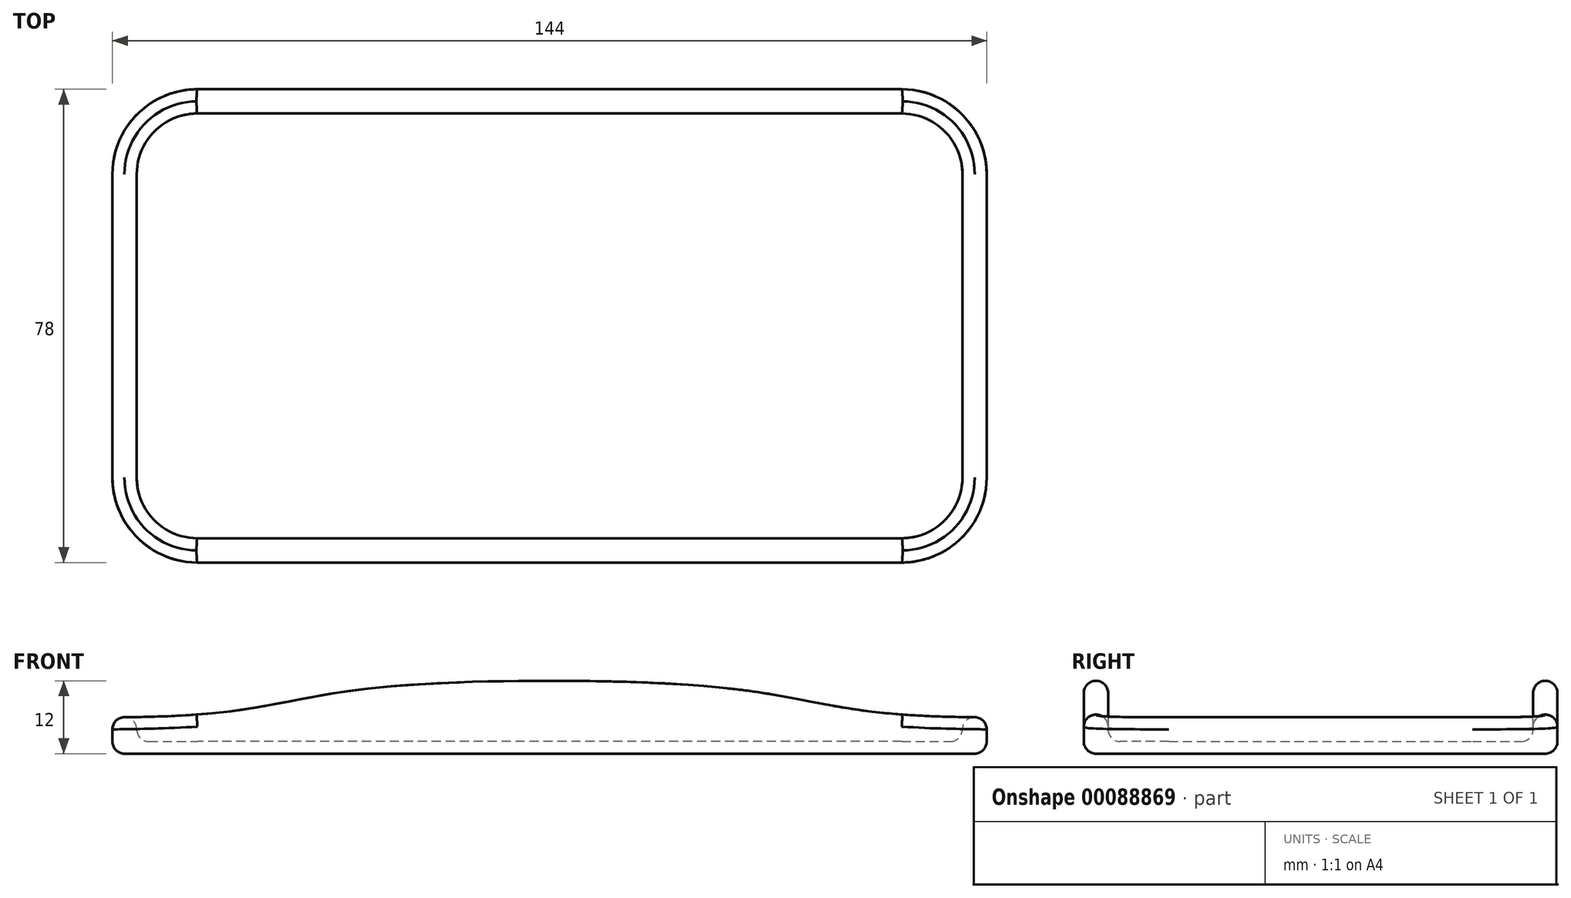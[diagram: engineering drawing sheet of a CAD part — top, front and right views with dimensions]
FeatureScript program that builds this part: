
annotation { "Feature Type Name" : "Feature", "Feature Type Description" : "" }
export const myFeature = defineFeature(function(context is Context, id is Id, definition is map)
    precondition{}
    {
        {
            var Q0;
            Q0=qCreatedBy(makeId("Top.planeOp"),FACE);
            var sketch = newSketch(context, id + "F0", { "sketchPlane" : qUnion([Q0])});
            skLineSegment(sketch, "E0.bottom", {"start": v(58, -35) * mm, "end": v(-58, -35) * mm});
            skLineSegment(sketch, "E0.top", {"start": v(58, 35) * mm, "end": v(-58, 35) * mm});
            skLineSegment(sketch, "E0.left", {"start": v(68, -25) * mm, "end": v(68, 25) * mm});
            skLineSegment(sketch, "E0.right", {"start": v(-68, -25) * mm, "end": v(-68, 25) * mm});
            skPoint(sketch, "E0.middle", {"position": v(0, 0) * mm});
            skPoint(sketch, "E1.visualSharp", {"position": v(-68, 35) * mm});
            skArc(sketch, "E1.filletArc", {"start": v(-58, 35) * mm, "mid": v(-65.07, 32.07) * mm, "end": v(-68, 25) * mm});
            skPoint(sketch, "E2.visualSharp", {"position": v(68, 35) * mm});
            skArc(sketch, "E2.filletArc", {"start": v(68, 25) * mm, "mid": v(65.07, 32.07) * mm, "end": v(58, 35) * mm});
            skPoint(sketch, "E3.visualSharp", {"position": v(68, -35) * mm});
            skArc(sketch, "E3.filletArc", {"start": v(58, -35) * mm, "mid": v(65.07, -32.07) * mm, "end": v(68, -25) * mm});
            skPoint(sketch, "E4.visualSharp", {"position": v(-68, -35) * mm});
            skArc(sketch, "E4.filletArc", {"start": v(-68, -25) * mm, "mid": v(-65.07, -32.07) * mm, "end": v(-58, -35) * mm});
            skArc(sketch, "E5.0", {"start": v(72, 25) * mm, "mid": v(67.9, 34.9) * mm, "end": v(58, 39) * mm});
            skLineSegment(sketch, "E5.1", {"start": v(72, -25) * mm, "end": v(72, 25) * mm});
            skLineSegment(sketch, "E5.2", {"start": v(58, 39) * mm, "end": v(-58, 39) * mm});
            skArc(sketch, "E5.3", {"start": v(58, -39) * mm, "mid": v(67.9, -34.9) * mm, "end": v(72, -25) * mm});
            skArc(sketch, "E5.4", {"start": v(-58, 39) * mm, "mid": v(-67.9, 34.9) * mm, "end": v(-72, 25) * mm});
            skLineSegment(sketch, "E5.5", {"start": v(-72, -25) * mm, "end": v(-72, 25) * mm});
            skArc(sketch, "E5.6", {"start": v(-72, -25) * mm, "mid": v(-67.9, -34.9) * mm, "end": v(-58, -39) * mm});
            skLineSegment(sketch, "E5.7", {"start": v(58, -39) * mm, "end": v(-58, -39) * mm});
            skSolve(sketch);
        }
        {
            var Q0;
            Q0=makeQuery(id+"F0.imprint","IMPRINT",FACE,{"disambiguationData":[TD([[makeQuery(id+"F0.imprint","IMPRINT",EDGE,{"derivedFrom":sQuery(id+"F0.wireOp",EDGE,"E0.bottom")}),-1.0]])]});
            extrude(context, id + "F1", {"entities" : qUnion([Q0]), "depth" : 2 * mm});
        }
        {
            var Q0;
            Q0=makeQuery(id+"F0.imprint","IMPRINT",FACE,{"disambiguationData":[TD([[makeQuery(id+"F0.imprint","IMPRINT",EDGE,{"derivedFrom":sQuery(id+"F0.wireOp",EDGE,"E0.bottom")}),1.0]])]});
            extrude(context, id + "F2", {"entities" : qUnion([Q0]), "operationType" : NewBodyOperationType.ADD, "depth" : 12 * mm});
        }
        {
            var Q0;
            Q0=qCreatedBy(makeId("Front.planeOp"),FACE);
            var sketch = newSketch(context, id + "F3", { "sketchPlane" : qUnion([Q0])});
            skLineSegment(sketch, "E6.0", {"start": v(58, 12) * mm, "end": v(-58, 12) * mm});
            skLineSegment(sketch, "E7.0", {"start": v(72, 0) * mm, "end": v(-72, 0) * mm});
            skLineSegment(sketch, "E8.0", {"start": v(72, 12) * mm, "end": v(72, 0) * mm});
            skLineSegment(sketch, "E9.0", {"start": v(-72, 12) * mm, "end": v(-72, 0) * mm});
            skFitSpline(sketch, "E10", {"points": [v(-72, 6) * mm, v(0, 12) * mm], "startDerivative": vector(102.55, 0) * mm, "endDerivative": vector(141.46, 0) * mm});
            skLineSegment(sketch, "E11", {"start": v(0, 12) * mm, "end": v(0, 0) * mm, "construction": true});
            skFitSpline(sketch, "E12.MirrorCS", {"points": [v(72, 6) * mm, v(0, 12) * mm], "startDerivative": vector(-102.55, 0) * mm, "endDerivative": vector(-141.46, 0) * mm});
            skPoint(sketch, "E13.orphan", {"position": v(-58, 0) * mm});
            skPoint(sketch, "E14.orphan", {"position": v(58, 0) * mm});
            skSolve(sketch);
        }
        {
            var Q0;
            {var subQ2=sQuery(id+"F3.wireOp",EDGE,"E7.0");Q0=makeQuery(id+"F3.imprint","IMPRINT",FACE,{"disambiguationData":[TD([[makeQuery(id+"F3.imprint","IMPRINT",EDGE,{"derivedFrom":subQ2}),-1.0]])]});}
            extrude(context, id + "F4", {"entities" : qUnion([Q0]), "operationType" : NewBodyOperationType.INTERSECT, "endBound" : BoundingType.SYMMETRIC, "depth" : 99 * mm});
        }
        {
            var Q0;
            Q0=makeQuery(id+"F2.opExtrude","SWEPT_FACE",FACE,{"disambiguationData":[OSD([sQuery(id+"F0.wireOp",EDGE,"E3.filletArc")])]});
            var Q1;
            Q1=makeQuery(id+"F2.opExtrude","SWEPT_FACE",FACE,{"disambiguationData":[OSD([sQuery(id+"F0.wireOp",EDGE,"E4.filletArc")])]});
            var Q2;
            Q2=makeQuery(id+"F2.opExtrude","SWEPT_FACE",FACE,{"disambiguationData":[OSD([sQuery(id+"F0.wireOp",EDGE,"E5.0")])]});
            fillet(context, id + "F5", {"entities" : qUnion([Q0, Q1, Q2]), "radius" : 2 * mm, "tangentPropagation" : true, "allowEdgeOverflow" : false});
        }
    });
